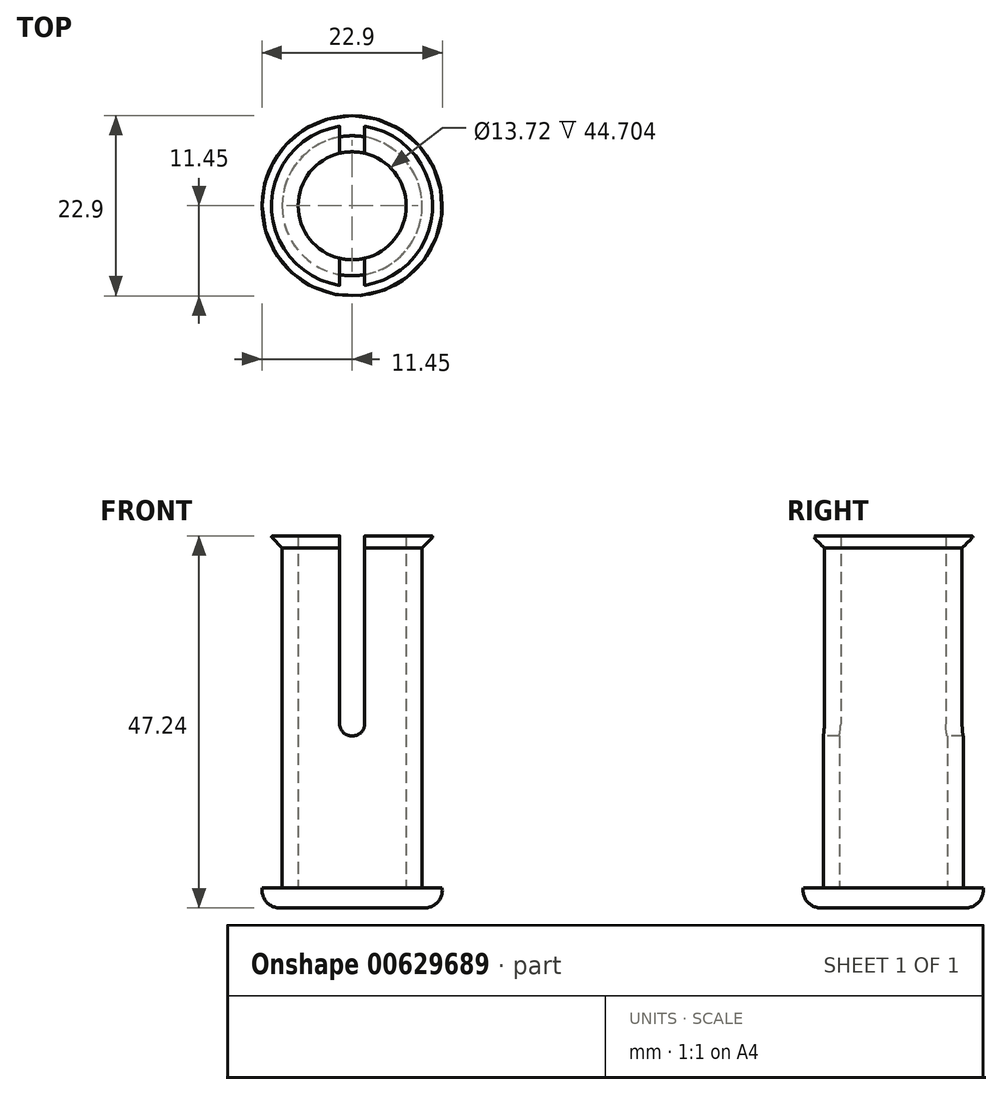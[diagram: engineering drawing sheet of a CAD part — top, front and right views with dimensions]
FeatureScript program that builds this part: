
annotation { "Feature Type Name" : "Feature", "Feature Type Description" : "" }
export const myFeature = defineFeature(function(context is Context, id is Id, definition is map)
    precondition{}
    {
        {
            var Q0;
            Q0=qCreatedBy(makeId("Top.planeOp"),FACE);
            var sketch = newSketch(context, id + "F0", { "sketchPlane" : qUnion([Q0])});
            skCircle(sketch, "E0", {"center": v(0, 0) * mm, "radius": 8.9 * mm});
            skCircle(sketch, "E1", {"center": v(0, 0) * mm, "radius": 6.86 * mm});
            skSolve(sketch);
        }
        {
            var Q0;
            Q0 = qSketchRegion(id + "F0", true);
            extrude(context, id + "F1", {"entities" : qUnion([Q0]), "depth" : 43.18 * mm, "offsetDistance" : 25.4 * mm});
        }
        {
            var Q0;
            Q0=qCreatedBy(makeId("Right.planeOp"),FACE);
            var sketch = newSketch(context, id + "F2", { "sketchPlane" : qUnion([Q0])});
            skLineSegment(sketch, "E2", {"start": v(8.9, 43.18) * mm, "end": v(10.41, 44.7) * mm});
            skLineSegment(sketch, "E3", {"start": v(10.41, 44.7) * mm, "end": v(6.86, 44.7) * mm});
            skLineSegment(sketch, "E4", {"start": v(6.86, 44.7) * mm, "end": v(6.86, 43.18) * mm});
            skLineSegment(sketch, "E5", {"start": v(6.86, 43.18) * mm, "end": v(8.9, 43.18) * mm});
            skLineSegment(sketch, "E6.0", {"start": v(-6.86, 43.18) * mm, "end": v(6.86, 43.18) * mm, "construction": true});
            skLineSegment(sketch, "E7", {"start": v(8.9, 0) * mm, "end": v(11.43, 0) * mm});
            skLineSegment(sketch, "E8", {"start": v(11.43, 0) * mm, "end": v(9.21, -2.54) * mm, "construction": true});
            skLineSegment(sketch, "E9", {"start": v(9.21, -2.54) * mm, "end": v(0, -2.54) * mm});
            skLineSegment(sketch, "E10", {"start": v(0, -2.54) * mm, "end": v(0, 0) * mm});
            skLineSegment(sketch, "E11", {"start": v(0, 0) * mm, "end": v(8.9, 0) * mm});
            skArc(sketch, "E12", {"start": v(9.21, -2.54) * mm, "mid": v(10.9, -1.77) * mm, "end": v(11.43, 0) * mm});
            skLineSegment(sketch, "E13.0", {"start": v(-8.9, 43.18) * mm, "end": v(8.9, 43.18) * mm, "construction": true});
            skSolve(sketch);
        }
        {
            var Q0;
            Q0 = qSketchRegion(id + "F2", true);
            var Q1;
            Q1=sQuery(id+"F2.wireOp",EDGE,"E10");
            revolve(context, id + "F3", {"operationType" : NewBodyOperationType.ADD, "entities" : qUnion([Q0]), "axis" : qUnion([Q1]), "revolveType" : RevolveType.FULL});
        }
        {
            var Q0;
            Q0=makeQuery(id+"F3.opRevolve","SWEPT_FACE",FACE,{"disambiguationData":[OSD([sQuery(id+"F2.wireOp",EDGE,"E3")])]});
            var sketch = newSketch(context, id + "F4", { "sketchPlane" : qUnion([Q0])});
            skLineSegment(sketch, "E14.bottom", {"start": v(1.59, 15.24) * mm, "end": v(-1.59, 15.24) * mm});
            skLineSegment(sketch, "E14.top", {"start": v(1.59, -15.24) * mm, "end": v(-1.59, -15.24) * mm});
            skLineSegment(sketch, "E14.left", {"start": v(1.59, 15.24) * mm, "end": v(1.59, -15.24) * mm});
            skLineSegment(sketch, "E14.right", {"start": v(-1.59, 15.24) * mm, "end": v(-1.59, -15.24) * mm});
            skPoint(sketch, "E14.middle", {"position": v(0, 0) * mm});
            skSolve(sketch);
        }
        {
            var Q0;
            Q0=makeQuery(id+"F3.opRevolve","SWEPT_EDGE",EDGE,{"disambiguationData":[OSD([sQuery(id+"F2.wireOp",EDGE,"E2"),sQuery(id+"F2.wireOp",EDGE,"E3")])]});
            fillet(context, id + "F5", {"entities" : qUnion([Q0]), "radius" : 0.13 * mm, "tangentPropagation" : true, "allowEdgeOverflow" : false});
        }
        {
            var Q0;
            Q0 = qSketchRegion(id + "F4", true);
            extrude(context, id + "F6", {"entities" : qUnion([Q0]), "operationType" : NewBodyOperationType.REMOVE, "oppositeDirection" : true, "depth" : 25.4 * mm, "offsetDistance" : 25.4 * mm});
        }
        {
            var Q0;
            Q0=makeQuery(id+"F6.boolean.opBoolean","COPY",EDGE,{"disambiguationData":[OD(0.0)],"derivedFrom":makeQuery(id+"F6.opExtrude","CAP_EDGE",EDGE,{"disambiguationData":[OSD([sQuery(id+"F4.wireOp",EDGE,"E14.right")])],"isStart":false})});
            var Q1;
            Q1=makeQuery(id+"F6.boolean.opBoolean","COPY",EDGE,{"disambiguationData":[OD(1.0)],"derivedFrom":makeQuery(id+"F6.opExtrude","CAP_EDGE",EDGE,{"disambiguationData":[OSD([sQuery(id+"F4.wireOp",EDGE,"E14.right")])],"isStart":false})});
            var Q2;
            Q2=makeQuery(id+"F6.boolean.opBoolean","COPY",EDGE,{"disambiguationData":[OD(1.0)],"derivedFrom":makeQuery(id+"F6.opExtrude","CAP_EDGE",EDGE,{"disambiguationData":[OSD([sQuery(id+"F4.wireOp",EDGE,"E14.left")])],"isStart":false})});
            var Q3;
            Q3=makeQuery(id+"F6.boolean.opBoolean","COPY",EDGE,{"disambiguationData":[OD(0.0)],"derivedFrom":makeQuery(id+"F6.opExtrude","CAP_EDGE",EDGE,{"disambiguationData":[OSD([sQuery(id+"F4.wireOp",EDGE,"E14.left")])],"isStart":false})});
            fillet(context, id + "F7", {"entities" : qUnion([Q0, Q1, Q2, Q3]), "radius" : 1.52 * mm, "tangentPropagation" : true, "allowEdgeOverflow" : false});
        }
    });
